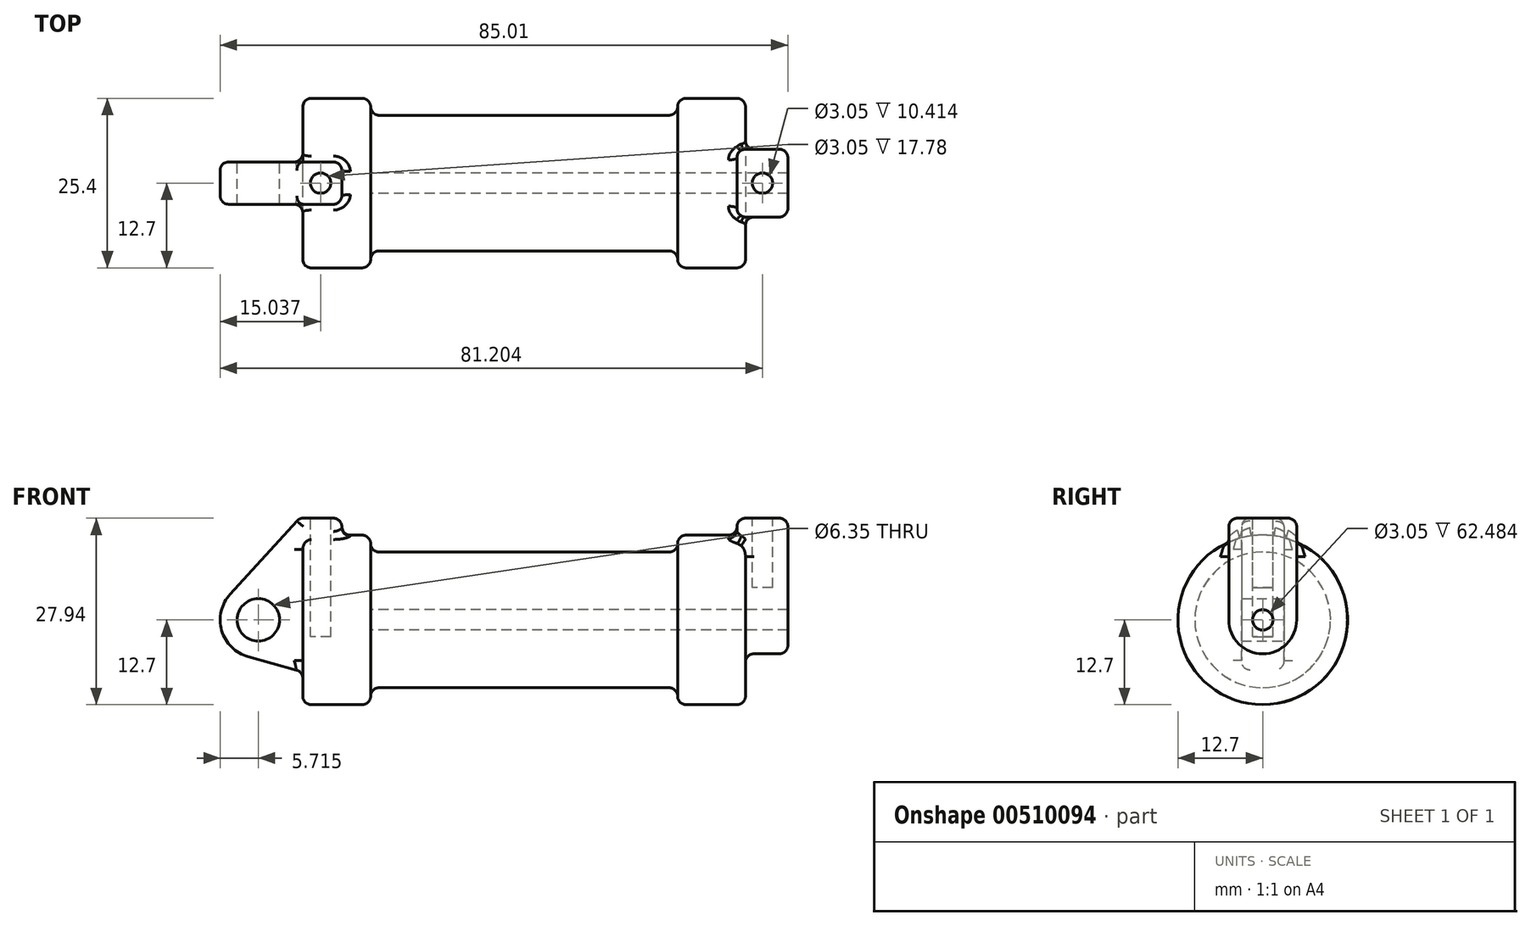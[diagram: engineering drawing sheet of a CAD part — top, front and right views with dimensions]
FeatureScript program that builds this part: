
annotation { "Feature Type Name" : "Feature", "Feature Type Description" : "" }
export const myFeature = defineFeature(function(context is Context, id is Id, definition is map)
    precondition{}
    {
        {
            var Q0;
            Q0=qCreatedBy(makeId("Front.planeOp"),FACE);
            var sketch = newSketch(context, id + "F0", { "sketchPlane" : qUnion([Q0])});
            skLineSegment(sketch, "E0", {"start": v(0, 0) * mm, "end": v(0, 12.7) * mm});
            skLineSegment(sketch, "E1", {"start": v(0, 12.7) * mm, "end": v(10.16, 12.7) * mm});
            skLineSegment(sketch, "E2", {"start": v(10.16, 12.7) * mm, "end": v(10.16, 10.16) * mm});
            skLineSegment(sketch, "E3", {"start": v(10.16, 10.16) * mm, "end": v(56.13, 10.16) * mm});
            skLineSegment(sketch, "E4", {"start": v(56.13, 10.16) * mm, "end": v(56.13, 12.7) * mm});
            skLineSegment(sketch, "E5", {"start": v(56.13, 12.7) * mm, "end": v(66.3, 12.7) * mm});
            skLineSegment(sketch, "E6", {"start": v(66.3, 12.7) * mm, "end": v(66.3, 0) * mm});
            skLineSegment(sketch, "E7", {"start": v(66.3, 0) * mm, "end": v(0, 0) * mm});
            skLineSegment(sketch, "E8", {"start": v(5.84, 15.24) * mm, "end": v(-0.5, 15.24) * mm});
            skLineSegment(sketch, "E9", {"start": v(-0.5, 15.24) * mm, "end": v(-10.88, 3.85) * mm});
            skLineSegment(sketch, "E10", {"start": v(0, 0) * mm, "end": v(-6.65, 0) * mm});
            skCircle(sketch, "E11", {"center": v(-6.65, 0) * mm, "radius": 5.72 * mm});
            skCircle(sketch, "E12", {"center": v(-6.65, 0) * mm, "radius": 3.18 * mm});
            skLineSegment(sketch, "E13", {"start": v(5.84, 15.24) * mm, "end": v(5.84, -9.4) * mm});
            skLineSegment(sketch, "E14", {"start": v(5.84, -9.4) * mm, "end": v(-8.18, -5.5) * mm});
            skPoint(sketch, "E15.endSnap0", {"position": v(5.84, 2.92) * mm});
            skSolve(sketch);
        }
        {
            var Q0;
            {var subQ0=sQuery(id+"F0.wireOp",EDGE,"E2");Q0=makeQuery(id+"F0.imprint","IMPRINT",FACE,{"disambiguationData":[TD([[makeQuery(id+"F0.imprint","IMPRINT",EDGE,{"derivedFrom":subQ0}),-1.0]])]});}
            var Q1;
            {var subQ0=sQuery(id+"F0.wireOp",EDGE,"E0");Q1=makeQuery(id+"F0.imprint","IMPRINT",FACE,{"disambiguationData":[TD([[makeQuery(id+"F0.imprint","IMPRINT",EDGE,{"derivedFrom":subQ0}),-1.0]])]});}
            var Q2;
            Q2=sQuery(id+"F0.wireOp",EDGE,"E7");
            revolve(context, id + "F1", {"entities" : qUnion([Q0, Q1]), "axis" : qUnion([Q2]), "revolveType" : RevolveType.FULL});
        }
        {
            var Q0;
            {var subQ1=sQuery(id+"F0.wireOp",EDGE,"E0");Q0=makeQuery(id+"F0.imprint","IMPRINT",FACE,{"disambiguationData":[TD([[makeQuery(id+"F0.imprint","IMPRINT",EDGE,{"derivedFrom":subQ1}),1.0]])]});}
            var Q1;
            {var subQ5=sQuery(id+"F0.wireOp",EDGE,"E12");Q1=makeQuery(id+"F0.imprint","IMPRINT",FACE,{"disambiguationData":[TD([[makeQuery(id+"F0.imprint","IMPRINT",EDGE,{"derivedFrom":subQ5}),-1.0]])]});}
            var Q2;
            {var subQ0=sQuery(id+"F0.wireOp",EDGE,"E14");Q2=makeQuery(id+"F0.imprint","IMPRINT",FACE,{"disambiguationData":[TD([[makeQuery(id+"F0.imprint","IMPRINT",EDGE,{"derivedFrom":subQ0}),-1.0]])]});}
            var Q3;
            {var subQ0=sQuery(id+"F0.wireOp",EDGE,"E0");Q3=makeQuery(id+"F0.imprint","IMPRINT",FACE,{"disambiguationData":[TD([[makeQuery(id+"F0.imprint","IMPRINT",EDGE,{"derivedFrom":subQ0}),-1.0]])]});}
            extrude(context, id + "F2", {"entities" : qUnion([Q0, Q1, Q2, Q3]), "operationType" : NewBodyOperationType.ADD, "endBound" : BoundingType.SYMMETRIC, "depth" : 6.35 * mm});
        }
        {
            var Q0;
            Q0=makeQuery(id+"F1.opRevolve","SWEPT_FACE",FACE,{"disambiguationData":[OSD([sQuery(id+"F0.wireOp",EDGE,"E6")])]});
            var sketch = newSketch(context, id + "F3", { "sketchPlane" : qUnion([Q0])});
            skCircle(sketch, "E16", {"center": v(0, 0) * mm, "radius": 1.52 * mm});
            skCircle(sketch, "E17", {"center": v(0, 0) * mm, "radius": 5.08 * mm});
            skLineSegment(sketch, "E18", {"start": v(5.08, 0) * mm, "end": v(5.08, 15.24) * mm});
            skLineSegment(sketch, "E19", {"start": v(5.08, 15.24) * mm, "end": v(-5.08, 15.24) * mm});
            skLineSegment(sketch, "E20", {"start": v(-5.08, 15.24) * mm, "end": v(-5.08, 0) * mm});
            skSolve(sketch);
        }
        {
            var Q0;
            {var subQ0=sQuery(id+"F3.wireOp",EDGE,"E18");var subQ1=sQuery(id+"F3.wireOp",EDGE,"E17");var subQ2=makeQuery(id+"F3.imprint","INTERSECT",VERTEX,{"derivedFrom":[subQ1,subQ0]});Q0=makeQuery(id+"F3.imprint","IMPRINT",FACE,{"disambiguationData":[TD([[makeQuery(id+"F3.imprint","IMPRINT",EDGE,{"disambiguationData":[TD([[subQ2,-1.0]])],"derivedFrom":subQ1}),-1.0]])]});}
            var Q1;
            {var subQ0=sQuery(id+"F3.wireOp",EDGE,"E19");Q1=makeQuery(id+"F3.imprint","IMPRINT",FACE,{"disambiguationData":[TD([[makeQuery(id+"F3.imprint","IMPRINT",EDGE,{"derivedFrom":subQ0}),1.0]])]});}
            var Q2;
            Q2=makeQuery(id+"F3.imprint","IMPRINT",FACE,{"disambiguationData":[TD([[makeQuery(id+"F3.imprint","IMPRINT",EDGE,{"derivedFrom":sQuery(id+"F3.wireOp",EDGE,"E16")}),-1.0]])]});
            extrude(context, id + "F4", {"entities" : qUnion([Q0, Q1, Q2]), "operationType" : NewBodyOperationType.ADD, "depth" : 6.35 * mm, "hasSecondDirection" : true, "secondDirectionOppositeDirection" : true, "secondDirectionDepth" : 1.27 * mm});
        }
        {
            var Q0;
            Q0=makeQuery(id+"F3.imprint","IMPRINT",FACE,{"disambiguationData":[TD([[makeQuery(id+"F3.imprint","IMPRINT",EDGE,{"derivedFrom":sQuery(id+"F3.wireOp",EDGE,"E16")}),1.0]])]});
            var Q1;
            Q1=makeQuery(id+"F1.opRevolve","SWEPT_FACE",FACE,{"disambiguationData":[OSD([sQuery(id+"F0.wireOp",EDGE,"E2")])]});
            extrude(context, id + "F5", {"entities" : qUnion([Q0]), "operationType" : NewBodyOperationType.REMOVE, "endBound" : BoundingType.UP_TO_SURFACE, "oppositeDirection" : true, "endBoundEntityFace" : qUnion([Q1]), "depth" : 25.4 * mm});
        }
        {
            var Q0;
            Q0=makeQuery(id+"F2.opExtrude","SWEPT_FACE",FACE,{"disambiguationData":[OSD([sQuery(id+"F0.wireOp",EDGE,"E8")])]});
            var sketch = newSketch(context, id + "F6", { "sketchPlane" : qUnion([Q0])});
            skCircle(sketch, "E21", {"center": v(2.67, 0) * mm, "radius": 1.52 * mm});
            skPoint(sketch, "E21.centerSnap0", {"position": v(-0.5, 0) * mm});
            skPoint(sketch, "E21.centerSnap1", {"position": v(2.67, 3.18) * mm});
            skSolve(sketch);
        }
        {
            var Q0;
            Q0=makeQuery(id+"F4.opExtrude","SWEPT_FACE",FACE,{"disambiguationData":[OSD([sQuery(id+"F3.wireOp",EDGE,"E19")])]});
            var sketch = newSketch(context, id + "F7", { "sketchPlane" : qUnion([Q0])});
            skCircle(sketch, "E22", {"center": v(68.83, 0) * mm, "radius": 1.52 * mm});
            skPoint(sketch, "E22.centerSnap0", {"position": v(65.02, 0) * mm});
            skPoint(sketch, "E22.centerSnap1", {"position": v(68.83, -5.08) * mm});
            skSolve(sketch);
        }
        {
            var Q0;
            Q0=makeQuery(id+"F7.imprint","IMPRINT",FACE,{"disambiguationData":[TD([[makeQuery(id+"F7.imprint","IMPRINT",EDGE,{"derivedFrom":sQuery(id+"F7.wireOp",EDGE,"E22")}),1.0]])]});
            extrude(context, id + "F8", {"entities" : qUnion([Q0]), "operationType" : NewBodyOperationType.REMOVE, "oppositeDirection" : true, "depth" : 10.4 * mm});
        }
        {
            var Q0;
            Q0=makeQuery(id+"F6.imprint","IMPRINT",FACE,{"disambiguationData":[TD([[makeQuery(id+"F6.imprint","IMPRINT",EDGE,{"derivedFrom":sQuery(id+"F6.wireOp",EDGE,"E21")}),1.0]])]});
            extrude(context, id + "F9", {"entities" : qUnion([Q0]), "operationType" : NewBodyOperationType.REMOVE, "oppositeDirection" : true, "depth" : 17.78 * mm});
        }
        {
            var Q0;
            Q0=makeQuery(id+"F1.opRevolve","SWEPT_EDGE",EDGE,{"disambiguationData":[OSD([sQuery(id+"F0.wireOp",EDGE,"E3"),sQuery(id+"F0.wireOp",EDGE,"E4")])]});
            var Q1;
            Q1=makeQuery(id+"F1.opRevolve","SWEPT_EDGE",EDGE,{"disambiguationData":[OSD([sQuery(id+"F0.wireOp",EDGE,"E4"),sQuery(id+"F0.wireOp",EDGE,"E5")])]});
            var Q2;
            Q2=makeQuery(id+"F1.opRevolve","SWEPT_EDGE",EDGE,{"disambiguationData":[OSD([sQuery(id+"F0.wireOp",EDGE,"E2"),sQuery(id+"F0.wireOp",EDGE,"E3")])]});
            var Q3;
            Q3=makeQuery(id+"F1.opRevolve","SWEPT_EDGE",EDGE,{"disambiguationData":[OSD([sQuery(id+"F0.wireOp",EDGE,"E1"),sQuery(id+"F0.wireOp",EDGE,"E2")])]});
            var Q4;
            Q4=makeQuery(id+"F1.opRevolve","SWEPT_EDGE",EDGE,{"disambiguationData":[OSD([sQuery(id+"F0.wireOp",EDGE,"E5"),sQuery(id+"F0.wireOp",EDGE,"E6")])]});
            var Q5;
            Q5=makeQuery(id+"F1.opRevolve","SWEPT_EDGE",EDGE,{"disambiguationData":[OSD([sQuery(id+"F0.wireOp",EDGE,"E0"),sQuery(id+"F0.wireOp",EDGE,"E1")])]});
            fillet(context, id + "F10", {"entities" : qUnion([Q0, Q1, Q2, Q3, Q4, Q5]), "radius" : 1.27 * mm, "tangentPropagation" : true, "allowEdgeOverflow" : false});
        }
        {
            var Q0;
            Q0=makeQuery(id+"F2.opExtrude","CAP_EDGE",EDGE,{"disambiguationData":[OSD([sQuery(id+"F0.wireOp",EDGE,"E9")])],"isStart":true});
            var Q1;
            Q1=makeQuery(id+"F2.opExtrude","CAP_EDGE",EDGE,{"disambiguationData":[OSD([sQuery(id+"F0.wireOp",EDGE,"E8")])],"isStart":true});
            var Q2;
            Q2=makeQuery(id+"F2.opExtrude","CAP_EDGE",EDGE,{"disambiguationData":[OSD([sQuery(id+"F0.wireOp",EDGE,"E9")])],"isStart":false});
            var Q3;
            Q3=makeQuery(id+"F2.opExtrude","SWEPT_EDGE",EDGE,{"disambiguationData":[OSD([sQuery(id+"F0.wireOp",EDGE,"E8"),sQuery(id+"F0.wireOp",EDGE,"E13")])]});
            var Q4;
            Q4=makeQuery(id+"F2.opExtrude","CAP_EDGE",EDGE,{"disambiguationData":[OSD([sQuery(id+"F0.wireOp",EDGE,"E8")])],"isStart":false});
            fillet(context, id + "F11", {"entities" : qUnion([Q0, Q1, Q2, Q3, Q4]), "radius" : 1.27 * mm, "tangentPropagation" : true, "allowEdgeOverflow" : false});
        }
        {
            var Q0;
            Q0=makeQuery(id+"F4.boolean.opBoolean","INTERSECT",EDGE,{"derivedFrom":[makeQuery(id+"F1.opRevolve","SWEPT_FACE",FACE,{"disambiguationData":[OSD([sQuery(id+"F0.wireOp",EDGE,"E5")])]}),makeQuery(id+"F4.opExtrude","CAP_FACE",FACE,{"disambiguationData":[OSD([sQuery(id+"F3.wireOp",EDGE,"E16"),sQuery(id+"F3.wireOp",EDGE,"E17"),sQuery(id+"F3.wireOp",EDGE,"E18"),sQuery(id+"F3.wireOp",EDGE,"E19"),sQuery(id+"F3.wireOp",EDGE,"E20")])],"isStart":true})]});
            var Q1;
            Q1=makeQuery(id+"F4.boolean.opBoolean","INTERSECT",EDGE,{"derivedFrom":[makeQuery(id+"F1.opRevolve","SWEPT_FACE",FACE,{"disambiguationData":[OSD([sQuery(id+"F0.wireOp",EDGE,"E6")])]}),makeQuery(id+"F4.opExtrude","SWEPT_FACE",FACE,{"disambiguationData":[OSD([sQuery(id+"F3.wireOp",EDGE,"E18")])]})]});
            var Q2;
            Q2=makeQuery(id+"F4.opExtrude","CAP_EDGE",EDGE,{"disambiguationData":[OSD([sQuery(id+"F3.wireOp",EDGE,"E20")])],"isStart":false});
            var Q3;
            Q3=makeQuery(id+"F4.opExtrude","CAP_EDGE",EDGE,{"disambiguationData":[OSD([sQuery(id+"F3.wireOp",EDGE,"E19")])],"isStart":false});
            var Q4;
            Q4=makeQuery(id+"F4.opExtrude","CAP_EDGE",EDGE,{"disambiguationData":[OSD([sQuery(id+"F3.wireOp",EDGE,"E19")])],"isStart":true});
            var Q5;
            Q5=makeQuery(id+"F4.opExtrude","SWEPT_EDGE",EDGE,{"disambiguationData":[OSD([sQuery(id+"F3.wireOp",EDGE,"E18"),sQuery(id+"F3.wireOp",EDGE,"E19")])]});
            var Q6;
            Q6=makeQuery(id+"F4.opExtrude","SWEPT_EDGE",EDGE,{"disambiguationData":[OSD([sQuery(id+"F3.wireOp",EDGE,"E19"),sQuery(id+"F3.wireOp",EDGE,"E20")])]});
            var Q7;
            Q7=makeQuery(id+"F4.boolean.opBoolean","INTERSECT",EDGE,{"derivedFrom":[makeQuery(id+"F1.opRevolve","SWEPT_FACE",FACE,{"disambiguationData":[OSD([sQuery(id+"F0.wireOp",EDGE,"E6")])]}),makeQuery(id+"F4.opExtrude","SWEPT_FACE",FACE,{"disambiguationData":[OSD([sQuery(id+"F3.wireOp",EDGE,"E20")])]})]});
            var Q8;
            Q8=makeQuery(id+"F4.boolean.opBoolean","INTERSECT",EDGE,{"derivedFrom":[makeQuery(id+"F1.opRevolve","SWEPT_FACE",FACE,{"disambiguationData":[OSD([sQuery(id+"F0.wireOp",EDGE,"E6")])]}),makeQuery(id+"F4.opExtrude","SWEPT_FACE",FACE,{"disambiguationData":[OSD([sQuery(id+"F3.wireOp",EDGE,"E17")])]})]});
            var Q9;
            Q9=makeQuery(id+"F10.opFillet","BLEND_EDGE",EDGE,{"blendedFrom":[makeQuery(id+"F1.opRevolve","SWEPT_EDGE",EDGE,{"disambiguationData":[OSD([sQuery(id+"F0.wireOp",EDGE,"E5"),sQuery(id+"F0.wireOp",EDGE,"E6")])]}),makeQuery(id+"F4.opExtrude","SWEPT_FACE",FACE,{"disambiguationData":[OSD([sQuery(id+"F3.wireOp",EDGE,"E18")])]})],"blendedInto":[makeQuery(id+"F4.opExtrude","SWEPT_FACE",FACE,{"disambiguationData":[OSD([sQuery(id+"F3.wireOp",EDGE,"E18")])]})]});
            var Q10;
            Q10=makeQuery(id+"F10.opFillet","BLEND_EDGE",EDGE,{"blendedFrom":[makeQuery(id+"F1.opRevolve","SWEPT_EDGE",EDGE,{"disambiguationData":[OSD([sQuery(id+"F0.wireOp",EDGE,"E5"),sQuery(id+"F0.wireOp",EDGE,"E6")])]}),makeQuery(id+"F4.opExtrude","SWEPT_FACE",FACE,{"disambiguationData":[OSD([sQuery(id+"F3.wireOp",EDGE,"E20")])]})],"blendedInto":[makeQuery(id+"F4.opExtrude","SWEPT_FACE",FACE,{"disambiguationData":[OSD([sQuery(id+"F3.wireOp",EDGE,"E20")])]})]});
            var Q11;
            Q11=makeQuery(id+"F4.opExtrude","CAP_EDGE",EDGE,{"disambiguationData":[OSD([sQuery(id+"F3.wireOp",EDGE,"E17")])],"isStart":false});
            var Q12;
            Q12=makeQuery(id+"F4.opExtrude","CAP_EDGE",EDGE,{"disambiguationData":[OSD([sQuery(id+"F3.wireOp",EDGE,"E18")])],"isStart":false});
            var Q13;
            Q13=makeQuery(id+"F4.opExtrude","CAP_EDGE",EDGE,{"disambiguationData":[OSD([sQuery(id+"F3.wireOp",EDGE,"E18")])],"isStart":true});
            var Q14;
            Q14=makeQuery(id+"F4.opExtrude","CAP_EDGE",EDGE,{"disambiguationData":[OSD([sQuery(id+"F3.wireOp",EDGE,"E20")])],"isStart":true});
            fillet(context, id + "F12", {"entities" : qUnion([Q0, Q1, Q2, Q3, Q4, Q5, Q6, Q7, Q8, Q9, Q10, Q11, Q12, Q13, Q14]), "radius" : 1.27 * mm, "tangentPropagation" : true, "allowEdgeOverflow" : false});
        }
        {
            var Q0;
            Q0=makeQuery(id+"F2.opExtrude","CAP_EDGE",EDGE,{"disambiguationData":[OSD([sQuery(id+"F0.wireOp",EDGE,"E13")])],"isStart":true});
            var Q1;
            Q1=makeQuery(id+"F2.opExtrude","CAP_EDGE",EDGE,{"disambiguationData":[OSD([sQuery(id+"F0.wireOp",EDGE,"E13")])],"isStart":false});
            var Q2;
            Q2=makeQuery(id+"FS1YXuvry7b2UE4_1.opBoolean","INTERSECT",EDGE,{"derivedFrom":[makeQuery(id+"F1.opRevolve","SWEPT_FACE",FACE,{"disambiguationData":[OSD([sQuery(id+"F0.wireOp",EDGE,"E1")])]}),makeQuery(id+"F2.opExtrude","SWEPT_FACE",FACE,{"disambiguationData":[OSD([sQuery(id+"F0.wireOp",EDGE,"E13")])]})]});
            var Q3;
            Q3=makeQuery(id+"FS1YXuvry7b2UE4_1.opBoolean","INTERSECT",EDGE,{"derivedFrom":[makeQuery(id+"F1.opRevolve","SWEPT_FACE",FACE,{"disambiguationData":[OSD([sQuery(id+"F0.wireOp",EDGE,"E1")])]}),makeQuery(id+"F2.opExtrude","CAP_FACE",FACE,{"disambiguationData":[OSD([sQuery(id+"F0.wireOp",EDGE,"E8"),sQuery(id+"F0.wireOp",EDGE,"E9"),sQuery(id+"F0.wireOp",EDGE,"E11"),sQuery(id+"F0.wireOp",EDGE,"E12"),sQuery(id+"F0.wireOp",EDGE,"E13"),sQuery(id+"F0.wireOp",EDGE,"E14")])],"isStart":true})]});
            var Q4;
            Q4=makeQuery(id+"FS1YXuvry7b2UE4_1.opBoolean","INTERSECT",EDGE,{"derivedFrom":[makeQuery(id+"F1.opRevolve","SWEPT_FACE",FACE,{"disambiguationData":[OSD([sQuery(id+"F0.wireOp",EDGE,"E0")])]}),makeQuery(id+"F2.opExtrude","CAP_FACE",FACE,{"disambiguationData":[OSD([sQuery(id+"F0.wireOp",EDGE,"E8"),sQuery(id+"F0.wireOp",EDGE,"E9"),sQuery(id+"F0.wireOp",EDGE,"E11"),sQuery(id+"F0.wireOp",EDGE,"E12"),sQuery(id+"F0.wireOp",EDGE,"E13"),sQuery(id+"F0.wireOp",EDGE,"E14")])],"isStart":true})]});
            var Q5;
            Q5=makeQuery(id+"FS1YXuvry7b2UE4_1.opBoolean","INTERSECT",EDGE,{"derivedFrom":[makeQuery(id+"F1.opRevolve","SWEPT_FACE",FACE,{"disambiguationData":[OSD([sQuery(id+"F0.wireOp",EDGE,"E0")])]}),makeQuery(id+"F2.opExtrude","CAP_FACE",FACE,{"disambiguationData":[OSD([sQuery(id+"F0.wireOp",EDGE,"E8"),sQuery(id+"F0.wireOp",EDGE,"E9"),sQuery(id+"F0.wireOp",EDGE,"E11"),sQuery(id+"F0.wireOp",EDGE,"E12"),sQuery(id+"F0.wireOp",EDGE,"E13"),sQuery(id+"F0.wireOp",EDGE,"E14")])],"isStart":false})]});
            var Q6;
            Q6=makeQuery(id+"F2.opExtrude","SWEPT_EDGE",EDGE,{"disambiguationData":[OSD([sQuery(id+"F0.wireOp",EDGE,"E8"),sQuery(id+"F0.wireOp",EDGE,"E9")])]});
            fillet(context, id + "F13", {"entities" : qUnion([Q0, Q1, Q2, Q3, Q4, Q5, Q6]), "radius" : 1.27 * mm, "tangentPropagation" : true, "allowEdgeOverflow" : false});
        }
        {
            var Q0;
            Q0=makeQuery(id+"F2.boolean.opBoolean","INTERSECT",EDGE,{"derivedFrom":[makeQuery(id+"F1.opRevolve","SWEPT_FACE",FACE,{"disambiguationData":[OSD([sQuery(id+"F0.wireOp",EDGE,"E0")])]}),makeQuery(id+"F2.opExtrude","CAP_FACE",FACE,{"disambiguationData":[OSD([sQuery(id+"F0.wireOp",EDGE,"E8"),sQuery(id+"F0.wireOp",EDGE,"E9"),sQuery(id+"F0.wireOp",EDGE,"E11"),sQuery(id+"F0.wireOp",EDGE,"E12"),sQuery(id+"F0.wireOp",EDGE,"E13"),sQuery(id+"F0.wireOp",EDGE,"E14")])],"isStart":false})]});
            fillet(context, id + "F14", {"entities" : qUnion([Q0]), "radius" : 1.27 * mm, "tangentPropagation" : true, "allowEdgeOverflow" : false});
        }
    });
